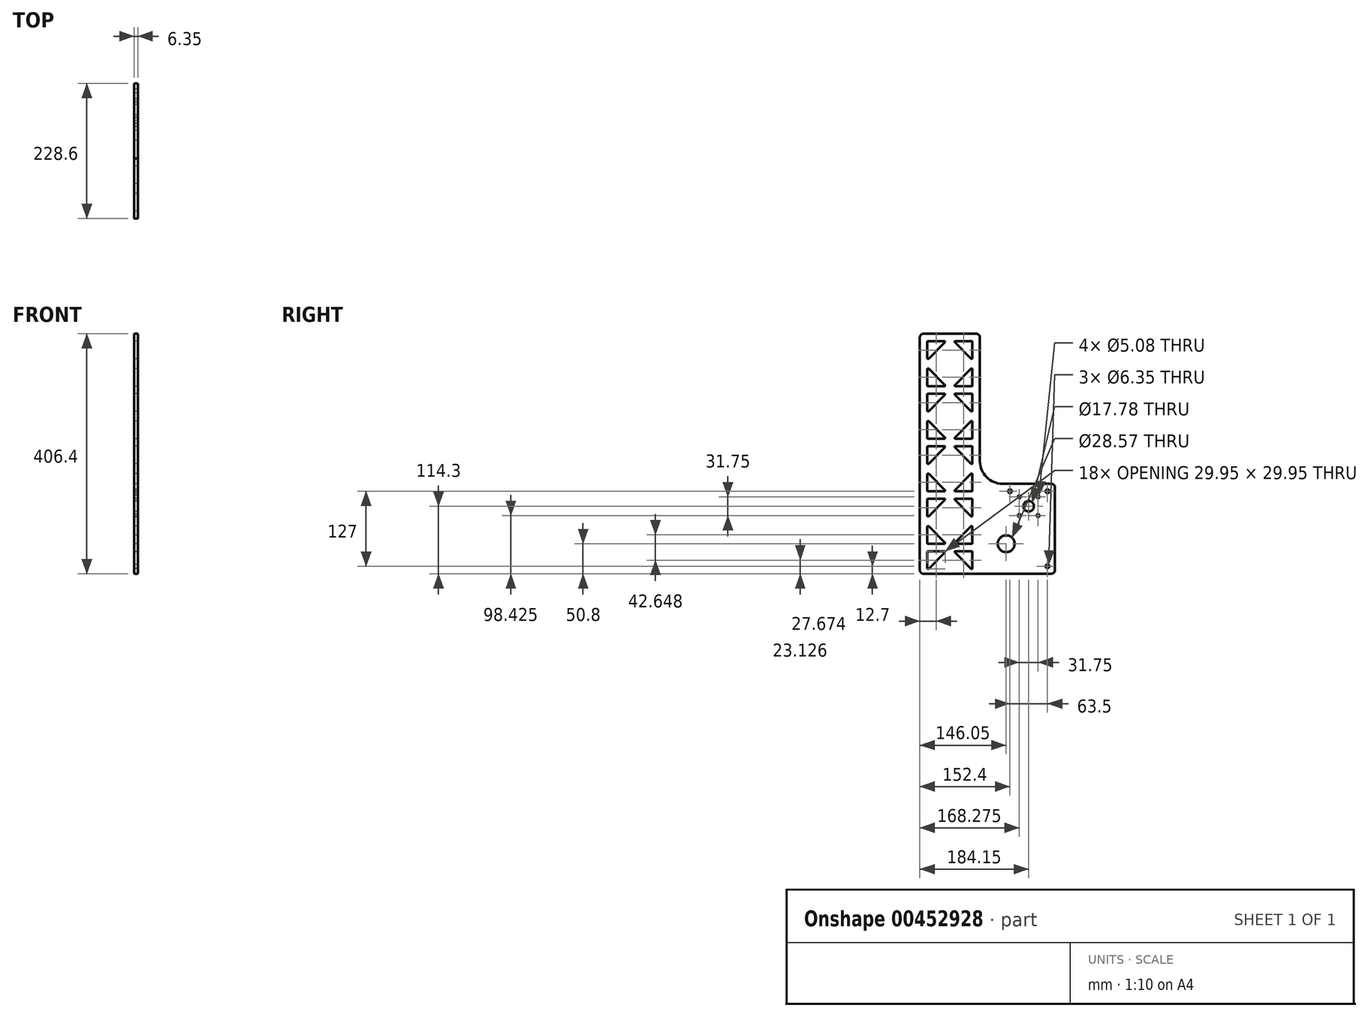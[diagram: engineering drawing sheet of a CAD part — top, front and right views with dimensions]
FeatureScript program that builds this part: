
annotation { "Feature Type Name" : "Feature", "Feature Type Description" : "" }
export const myFeature = defineFeature(function(context is Context, id is Id, definition is map)
    precondition{}
    {
        {
            var Q0;
            Q0=qCreatedBy(makeId("Right.planeOp"),FACE);
            var sketch = newSketch(context, id + "F0", { "sketchPlane" : qUnion([Q0])});
            skLineSegment(sketch, "E0.bottom", {"start": v(0, 0) * mm, "end": v(101.6, 0) * mm});
            skLineSegment(sketch, "E0.top", {"start": v(0, 406.4) * mm, "end": v(101.6, 406.4) * mm});
            skLineSegment(sketch, "E0.left", {"start": v(0, 0) * mm, "end": v(0, 406.4) * mm});
            skLineSegment(sketch, "E0.right", {"start": v(101.6, 0) * mm, "end": v(101.6, 406.4) * mm});
            skLineSegment(sketch, "E1.bottom", {"start": v(101.6, 0) * mm, "end": v(228.6, 0) * mm});
            skLineSegment(sketch, "E1.top", {"start": v(101.6, 152.4) * mm, "end": v(228.6, 152.4) * mm});
            skLineSegment(sketch, "E1.left", {"start": v(101.6, 0) * mm, "end": v(101.6, 152.4) * mm});
            skLineSegment(sketch, "E1.right", {"start": v(228.6, 0) * mm, "end": v(228.6, 152.4) * mm});
            skCircle(sketch, "E2", {"center": v(146.05, 50.8) * mm, "radius": 14.29 * mm});
            skCircle(sketch, "E3", {"center": v(146.05, 50.8) * mm, "radius": 50.8 * mm, "construction": true});
            skCircle(sketch, "E4", {"center": v(215.9, 12.7) * mm, "radius": 3.18 * mm});
            skCircle(sketch, "E5", {"center": v(215.9, 139.7) * mm, "radius": 3.18 * mm});
            skLineSegment(sketch, "E6", {"start": v(87.63, 393.7) * mm, "end": v(60.22, 393.7) * mm});
            skLineSegment(sketch, "E7", {"start": v(59.32, 391.53) * mm, "end": v(86.73, 364.12) * mm});
            skLineSegment(sketch, "E8", {"start": v(88.9, 365.02) * mm, "end": v(88.9, 392.43) * mm});
            skPoint(sketch, "E9.visualSharp", {"position": v(57.15, 393.7) * mm});
            skArc(sketch, "E9.filletArc", {"start": v(60.22, 393.7) * mm, "mid": v(59.04, 392.92) * mm, "end": v(59.32, 391.53) * mm});
            skPoint(sketch, "E10.visualSharp", {"position": v(88.9, 361.95) * mm});
            skArc(sketch, "E11.filletArc", {"start": v(86.73, 364.12) * mm, "mid": v(88.12, 363.84) * mm, "end": v(88.9, 365.02) * mm});
            skPoint(sketch, "E12.visualSharp", {"position": v(88.9, 393.7) * mm});
            skArc(sketch, "E12.filletArc", {"start": v(88.9, 392.43) * mm, "mid": v(88.53, 393.33) * mm, "end": v(87.63, 393.7) * mm});
            skPoint(sketch, "E13.startSnap0", {"position": v(50.8, 406.4) * mm});
            skLineSegment(sketch, "E14", {"start": v(50.8, 406.4) * mm, "end": v(50.8, -18.77) * mm, "construction": true});
            skPoint(sketch, "E14.endSnap0", {"position": v(50.8, 0) * mm});
            skArc(sketch, "E15.MirrorCS", {"start": v(12.7, 392.43) * mm, "mid": v(13.07, 393.33) * mm, "end": v(13.97, 393.7) * mm});
            skArc(sketch, "E16.MirrorCS", {"start": v(41.38, 393.7) * mm, "mid": v(42.56, 392.92) * mm, "end": v(42.28, 391.53) * mm});
            skPoint(sketch, "E17.MirrorP", {"position": v(12.7, 361.95) * mm});
            skLineSegment(sketch, "E18.MirrorCS", {"start": v(13.97, 393.7) * mm, "end": v(41.38, 393.7) * mm});
            skPoint(sketch, "E19.MirrorP", {"position": v(12.7, 393.7) * mm});
            skLineSegment(sketch, "E20.MirrorCS", {"start": v(42.28, 391.53) * mm, "end": v(14.87, 364.12) * mm});
            skPoint(sketch, "E21.MirrorP", {"position": v(44.45, 393.7) * mm});
            skArc(sketch, "E22.MirrorCS", {"start": v(14.87, 364.12) * mm, "mid": v(13.48, 363.84) * mm, "end": v(12.7, 365.02) * mm});
            skLineSegment(sketch, "E23.MirrorCS", {"start": v(12.7, 365.02) * mm, "end": v(12.7, 392.43) * mm});
            skLineSegment(sketch, "E24", {"start": v(-14.42, 355.6) * mm, "end": v(137.53, 355.6) * mm, "construction": true});
            skArc(sketch, "E25.MirrorCS", {"start": v(12.7, 318.77) * mm, "mid": v(13.07, 317.87) * mm, "end": v(13.97, 317.5) * mm});
            skArc(sketch, "E26.MirrorCS", {"start": v(60.22, 317.5) * mm, "mid": v(59.04, 318.28) * mm, "end": v(59.32, 319.67) * mm});
            skArc(sketch, "E27.MirrorCS", {"start": v(14.87, 347.08) * mm, "mid": v(13.48, 347.36) * mm, "end": v(12.7, 346.18) * mm});
            skArc(sketch, "E28.MirrorCS", {"start": v(41.38, 317.5) * mm, "mid": v(42.56, 318.28) * mm, "end": v(42.28, 319.67) * mm});
            skArc(sketch, "E29.MirrorCS", {"start": v(86.73, 347.08) * mm, "mid": v(88.12, 347.36) * mm, "end": v(88.9, 346.18) * mm});
            skArc(sketch, "E30.MirrorCS", {"start": v(88.9, 318.77) * mm, "mid": v(88.53, 317.87) * mm, "end": v(87.63, 317.5) * mm});
            skPoint(sketch, "E31.MirrorP", {"position": v(12.7, 349.25) * mm});
            skPoint(sketch, "E32.MirrorP", {"position": v(88.9, 349.25) * mm});
            skPoint(sketch, "E33.MirrorP", {"position": v(12.7, 317.5) * mm});
            skPoint(sketch, "E34.MirrorP", {"position": v(44.45, 317.5) * mm});
            skLineSegment(sketch, "E35.MirrorCS", {"start": v(50.8, 304.8) * mm, "end": v(50.8, 729.97) * mm, "construction": true});
            skPoint(sketch, "E36.MirrorP", {"position": v(88.9, 317.5) * mm});
            skLineSegment(sketch, "E37.MirrorCS", {"start": v(12.7, 346.18) * mm, "end": v(12.7, 318.77) * mm});
            skLineSegment(sketch, "E38.MirrorCS", {"start": v(88.9, 346.18) * mm, "end": v(88.9, 318.77) * mm});
            skLineSegment(sketch, "E39.MirrorCS", {"start": v(42.28, 319.67) * mm, "end": v(14.87, 347.08) * mm});
            skLineSegment(sketch, "E40.MirrorCS", {"start": v(13.97, 317.5) * mm, "end": v(41.38, 317.5) * mm});
            skPoint(sketch, "E41.MirrorP", {"position": v(57.15, 317.5) * mm});
            skLineSegment(sketch, "E42.MirrorCS", {"start": v(87.63, 317.5) * mm, "end": v(60.22, 317.5) * mm});
            skLineSegment(sketch, "E43.MirrorCS", {"start": v(59.32, 319.67) * mm, "end": v(86.73, 347.08) * mm});
            skPoint(sketch, "E44.0.1.0", {"position": v(44.45, 304.8) * mm});
            skLineSegment(sketch, "E44.0.1.1", {"start": v(12.7, 276.12) * mm, "end": v(12.7, 303.53) * mm});
            skPoint(sketch, "E44.0.1.2", {"position": v(12.7, 273.05) * mm});
            skPoint(sketch, "E44.0.1.3", {"position": v(12.7, 304.8) * mm});
            skLineSegment(sketch, "E44.0.1.4", {"start": v(42.28, 302.63) * mm, "end": v(14.87, 275.22) * mm});
            skLineSegment(sketch, "E44.0.1.5", {"start": v(13.97, 304.8) * mm, "end": v(41.38, 304.8) * mm});
            skPoint(sketch, "E44.0.1.6", {"position": v(12.7, 273.05) * mm});
            skArc(sketch, "E44.0.1.7", {"start": v(14.87, 275.22) * mm, "mid": v(13.48, 274.94) * mm, "end": v(12.7, 276.12) * mm});
            skArc(sketch, "E44.0.1.8", {"start": v(41.38, 304.8) * mm, "mid": v(42.56, 304.02) * mm, "end": v(42.28, 302.63) * mm});
            skArc(sketch, "E44.0.1.9", {"start": v(12.7, 303.53) * mm, "mid": v(13.07, 304.43) * mm, "end": v(13.97, 304.8) * mm});
            skPoint(sketch, "E44.0.1.10", {"position": v(44.45, 228.6) * mm});
            skLineSegment(sketch, "E44.0.1.11", {"start": v(13.97, 228.6) * mm, "end": v(41.38, 228.6) * mm});
            skPoint(sketch, "E44.0.1.12", {"position": v(12.7, 260.35) * mm});
            skLineSegment(sketch, "E44.0.1.13", {"start": v(42.28, 230.77) * mm, "end": v(14.87, 258.18) * mm});
            skPoint(sketch, "E44.0.1.14", {"position": v(12.7, 228.6) * mm});
            skLineSegment(sketch, "E44.0.1.15", {"start": v(12.7, 257.28) * mm, "end": v(12.7, 229.87) * mm});
            skPoint(sketch, "E44.0.1.16", {"position": v(12.7, 260.35) * mm});
            skArc(sketch, "E44.0.1.17", {"start": v(41.38, 228.6) * mm, "mid": v(42.56, 229.38) * mm, "end": v(42.28, 230.77) * mm});
            skArc(sketch, "E44.0.1.18", {"start": v(14.87, 258.18) * mm, "mid": v(13.48, 258.46) * mm, "end": v(12.7, 257.28) * mm});
            skArc(sketch, "E44.0.1.19", {"start": v(12.7, 229.87) * mm, "mid": v(13.07, 228.97) * mm, "end": v(13.97, 228.6) * mm});
            skPoint(sketch, "E44.0.1.20", {"position": v(57.15, 228.6) * mm});
            skPoint(sketch, "E44.0.1.21", {"position": v(88.9, 228.6) * mm});
            skLineSegment(sketch, "E44.0.1.22", {"start": v(59.32, 230.77) * mm, "end": v(86.73, 258.18) * mm});
            skLineSegment(sketch, "E44.0.1.23", {"start": v(87.63, 228.6) * mm, "end": v(60.22, 228.6) * mm});
            skPoint(sketch, "E44.0.1.24", {"position": v(88.9, 260.35) * mm});
            skLineSegment(sketch, "E44.0.1.25", {"start": v(88.9, 257.28) * mm, "end": v(88.9, 229.87) * mm});
            skPoint(sketch, "E44.0.1.26", {"position": v(88.9, 260.35) * mm});
            skArc(sketch, "E44.0.1.27", {"start": v(60.22, 228.6) * mm, "mid": v(59.04, 229.38) * mm, "end": v(59.32, 230.77) * mm});
            skArc(sketch, "E44.0.1.28", {"start": v(88.9, 229.87) * mm, "mid": v(88.53, 228.97) * mm, "end": v(87.63, 228.6) * mm});
            skArc(sketch, "E44.0.1.29", {"start": v(86.73, 258.18) * mm, "mid": v(88.12, 258.46) * mm, "end": v(88.9, 257.28) * mm});
            skLineSegment(sketch, "E44.0.1.30", {"start": v(88.9, 276.12) * mm, "end": v(88.9, 303.53) * mm});
            skLineSegment(sketch, "E44.0.1.31", {"start": v(59.32, 302.63) * mm, "end": v(86.73, 275.22) * mm});
            skLineSegment(sketch, "E44.0.1.32", {"start": v(87.63, 304.8) * mm, "end": v(60.22, 304.8) * mm});
            skPoint(sketch, "E44.0.1.33", {"position": v(88.9, 304.8) * mm});
            skPoint(sketch, "E44.0.1.34", {"position": v(88.9, 273.05) * mm});
            skPoint(sketch, "E44.0.1.35", {"position": v(57.15, 304.8) * mm});
            skPoint(sketch, "E44.0.1.36", {"position": v(88.9, 273.05) * mm});
            skArc(sketch, "E44.0.1.37", {"start": v(86.73, 275.22) * mm, "mid": v(88.12, 274.94) * mm, "end": v(88.9, 276.12) * mm});
            skArc(sketch, "E44.0.1.38", {"start": v(88.9, 303.53) * mm, "mid": v(88.53, 304.43) * mm, "end": v(87.63, 304.8) * mm});
            skArc(sketch, "E44.0.1.39", {"start": v(60.22, 304.8) * mm, "mid": v(59.04, 304.02) * mm, "end": v(59.32, 302.63) * mm});
            skPoint(sketch, "E44.0.2.0", {"position": v(44.45, 215.9) * mm});
            skLineSegment(sketch, "E44.0.2.1", {"start": v(12.7, 187.22) * mm, "end": v(12.7, 214.63) * mm});
            skPoint(sketch, "E44.0.2.2", {"position": v(12.7, 184.15) * mm});
            skPoint(sketch, "E44.0.2.3", {"position": v(12.7, 215.9) * mm});
            skLineSegment(sketch, "E44.0.2.4", {"start": v(42.28, 213.73) * mm, "end": v(14.87, 186.32) * mm});
            skLineSegment(sketch, "E44.0.2.5", {"start": v(13.97, 215.9) * mm, "end": v(41.38, 215.9) * mm});
            skPoint(sketch, "E44.0.2.6", {"position": v(12.7, 184.15) * mm});
            skArc(sketch, "E44.0.2.7", {"start": v(14.87, 186.32) * mm, "mid": v(13.48, 186.04) * mm, "end": v(12.7, 187.22) * mm});
            skArc(sketch, "E44.0.2.8", {"start": v(41.38, 215.9) * mm, "mid": v(42.56, 215.12) * mm, "end": v(42.28, 213.73) * mm});
            skArc(sketch, "E44.0.2.9", {"start": v(12.7, 214.63) * mm, "mid": v(13.07, 215.53) * mm, "end": v(13.97, 215.9) * mm});
            skPoint(sketch, "E44.0.2.10", {"position": v(44.45, 139.7) * mm});
            skLineSegment(sketch, "E44.0.2.11", {"start": v(13.97, 139.7) * mm, "end": v(41.38, 139.7) * mm});
            skPoint(sketch, "E44.0.2.12", {"position": v(12.7, 171.45) * mm});
            skLineSegment(sketch, "E44.0.2.13", {"start": v(42.28, 141.87) * mm, "end": v(14.87, 169.28) * mm});
            skPoint(sketch, "E44.0.2.14", {"position": v(12.7, 139.7) * mm});
            skLineSegment(sketch, "E44.0.2.15", {"start": v(12.7, 168.38) * mm, "end": v(12.7, 140.97) * mm});
            skPoint(sketch, "E44.0.2.16", {"position": v(12.7, 171.45) * mm});
            skArc(sketch, "E44.0.2.17", {"start": v(41.38, 139.7) * mm, "mid": v(42.56, 140.48) * mm, "end": v(42.28, 141.87) * mm});
            skArc(sketch, "E44.0.2.18", {"start": v(14.87, 169.28) * mm, "mid": v(13.48, 169.56) * mm, "end": v(12.7, 168.38) * mm});
            skArc(sketch, "E44.0.2.19", {"start": v(12.7, 140.97) * mm, "mid": v(13.07, 140.07) * mm, "end": v(13.97, 139.7) * mm});
            skPoint(sketch, "E44.0.2.20", {"position": v(57.15, 139.7) * mm});
            skPoint(sketch, "E44.0.2.21", {"position": v(88.9, 139.7) * mm});
            skLineSegment(sketch, "E44.0.2.22", {"start": v(59.32, 141.87) * mm, "end": v(86.73, 169.28) * mm});
            skLineSegment(sketch, "E44.0.2.23", {"start": v(87.63, 139.7) * mm, "end": v(60.22, 139.7) * mm});
            skPoint(sketch, "E44.0.2.24", {"position": v(88.9, 171.45) * mm});
            skLineSegment(sketch, "E44.0.2.25", {"start": v(88.9, 168.38) * mm, "end": v(88.9, 140.97) * mm});
            skPoint(sketch, "E44.0.2.26", {"position": v(88.9, 171.45) * mm});
            skArc(sketch, "E44.0.2.27", {"start": v(60.22, 139.7) * mm, "mid": v(59.04, 140.48) * mm, "end": v(59.32, 141.87) * mm});
            skArc(sketch, "E44.0.2.28", {"start": v(88.9, 140.97) * mm, "mid": v(88.53, 140.07) * mm, "end": v(87.63, 139.7) * mm});
            skArc(sketch, "E44.0.2.29", {"start": v(86.73, 169.28) * mm, "mid": v(88.12, 169.56) * mm, "end": v(88.9, 168.38) * mm});
            skLineSegment(sketch, "E44.0.2.30", {"start": v(88.9, 187.22) * mm, "end": v(88.9, 214.63) * mm});
            skLineSegment(sketch, "E44.0.2.31", {"start": v(59.32, 213.73) * mm, "end": v(86.73, 186.32) * mm});
            skLineSegment(sketch, "E44.0.2.32", {"start": v(87.63, 215.9) * mm, "end": v(60.22, 215.9) * mm});
            skPoint(sketch, "E44.0.2.33", {"position": v(88.9, 215.9) * mm});
            skPoint(sketch, "E44.0.2.34", {"position": v(88.9, 184.15) * mm});
            skPoint(sketch, "E44.0.2.35", {"position": v(57.15, 215.9) * mm});
            skPoint(sketch, "E44.0.2.36", {"position": v(88.9, 184.15) * mm});
            skArc(sketch, "E44.0.2.37", {"start": v(86.73, 186.32) * mm, "mid": v(88.12, 186.04) * mm, "end": v(88.9, 187.22) * mm});
            skArc(sketch, "E44.0.2.38", {"start": v(88.9, 214.63) * mm, "mid": v(88.53, 215.53) * mm, "end": v(87.63, 215.9) * mm});
            skArc(sketch, "E44.0.2.39", {"start": v(60.22, 215.9) * mm, "mid": v(59.04, 215.12) * mm, "end": v(59.32, 213.73) * mm});
            skLineSegment(sketch, "E44.direction1", {"start": v(12.7, 317.5) * mm, "end": v(12.65, 317.5) * mm, "construction": true});
            skLineSegment(sketch, "E44.direction2", {"start": v(12.7, 317.5) * mm, "end": v(12.7, 228.6) * mm, "construction": true});
            skPoint(sketch, "E45.0.0.3", {"position": v(44.45, 127) * mm});
            skLineSegment(sketch, "E45.1.0.3", {"start": v(12.7, 98.32) * mm, "end": v(12.7, 125.73) * mm});
            skPoint(sketch, "E45.4.0.3", {"position": v(12.7, 95.25) * mm});
            skPoint(sketch, "E45.5.0.3", {"position": v(12.7, 127) * mm});
            skLineSegment(sketch, "E45.6.0.3", {"start": v(42.28, 124.83) * mm, "end": v(14.87, 97.42) * mm});
            skLineSegment(sketch, "E45.9.0.3", {"start": v(13.97, 127) * mm, "end": v(41.38, 127) * mm});
            skPoint(sketch, "E45.12.0.3", {"position": v(12.7, 95.25) * mm});
            skArc(sketch, "E45.13.0.3", {"start": v(14.87, 97.42) * mm, "mid": v(13.48, 97.14) * mm, "end": v(12.7, 98.32) * mm});
            skArc(sketch, "E45.17.0.3", {"start": v(41.38, 127) * mm, "mid": v(42.56, 126.22) * mm, "end": v(42.28, 124.83) * mm});
            skArc(sketch, "E45.21.0.3", {"start": v(12.7, 125.73) * mm, "mid": v(13.07, 126.63) * mm, "end": v(13.97, 127) * mm});
            skPoint(sketch, "E45.25.0.3", {"position": v(44.45, 50.8) * mm});
            skLineSegment(sketch, "E45.26.0.3", {"start": v(13.97, 50.8) * mm, "end": v(41.38, 50.8) * mm});
            skPoint(sketch, "E45.29.0.3", {"position": v(12.7, 82.55) * mm});
            skLineSegment(sketch, "E45.30.0.3", {"start": v(42.28, 52.97) * mm, "end": v(14.87, 80.38) * mm});
            skPoint(sketch, "E45.33.0.3", {"position": v(12.7, 50.8) * mm});
            skLineSegment(sketch, "E45.34.0.3", {"start": v(12.7, 79.48) * mm, "end": v(12.7, 52.07) * mm});
            skPoint(sketch, "E45.37.0.3", {"position": v(12.7, 82.55) * mm});
            skArc(sketch, "E45.38.0.3", {"start": v(41.38, 50.8) * mm, "mid": v(42.56, 51.58) * mm, "end": v(42.28, 52.97) * mm});
            skArc(sketch, "E45.42.0.3", {"start": v(14.87, 80.38) * mm, "mid": v(13.48, 80.66) * mm, "end": v(12.7, 79.48) * mm});
            skArc(sketch, "E45.46.0.3", {"start": v(12.7, 52.07) * mm, "mid": v(13.07, 51.17) * mm, "end": v(13.97, 50.8) * mm});
            skPoint(sketch, "E45.50.0.3", {"position": v(57.15, 50.8) * mm});
            skPoint(sketch, "E45.51.0.3", {"position": v(88.9, 50.8) * mm});
            skLineSegment(sketch, "E45.52.0.3", {"start": v(59.32, 52.97) * mm, "end": v(86.73, 80.38) * mm});
            skLineSegment(sketch, "E45.55.0.3", {"start": v(87.63, 50.8) * mm, "end": v(60.22, 50.8) * mm});
            skPoint(sketch, "E45.58.0.3", {"position": v(88.9, 82.55) * mm});
            skLineSegment(sketch, "E45.59.0.3", {"start": v(88.9, 79.48) * mm, "end": v(88.9, 52.07) * mm});
            skPoint(sketch, "E45.62.0.3", {"position": v(88.9, 82.55) * mm});
            skArc(sketch, "E45.63.0.3", {"start": v(60.22, 50.8) * mm, "mid": v(59.04, 51.58) * mm, "end": v(59.32, 52.97) * mm});
            skArc(sketch, "E45.67.0.3", {"start": v(88.9, 52.07) * mm, "mid": v(88.53, 51.17) * mm, "end": v(87.63, 50.8) * mm});
            skArc(sketch, "E45.71.0.3", {"start": v(86.73, 80.38) * mm, "mid": v(88.12, 80.66) * mm, "end": v(88.9, 79.48) * mm});
            skLineSegment(sketch, "E45.75.0.3", {"start": v(88.9, 98.32) * mm, "end": v(88.9, 125.73) * mm});
            skLineSegment(sketch, "E45.78.0.3", {"start": v(59.32, 124.83) * mm, "end": v(86.73, 97.42) * mm});
            skLineSegment(sketch, "E45.81.0.3", {"start": v(87.63, 127) * mm, "end": v(60.22, 127) * mm});
            skPoint(sketch, "E45.84.0.3", {"position": v(88.9, 127) * mm});
            skPoint(sketch, "E45.85.0.3", {"position": v(88.9, 95.25) * mm});
            skPoint(sketch, "E45.86.0.3", {"position": v(57.15, 127) * mm});
            skPoint(sketch, "E45.87.0.3", {"position": v(88.9, 95.25) * mm});
            skArc(sketch, "E45.88.0.3", {"start": v(86.73, 97.42) * mm, "mid": v(88.12, 97.14) * mm, "end": v(88.9, 98.32) * mm});
            skArc(sketch, "E45.92.0.3", {"start": v(88.9, 125.73) * mm, "mid": v(88.53, 126.63) * mm, "end": v(87.63, 127) * mm});
            skArc(sketch, "E45.96.0.3", {"start": v(60.22, 127) * mm, "mid": v(59.04, 126.22) * mm, "end": v(59.32, 124.83) * mm});
            skPoint(sketch, "E45.0.0.4", {"position": v(44.45, 38.1) * mm});
            skLineSegment(sketch, "E45.1.0.4", {"start": v(12.7, 9.42) * mm, "end": v(12.7, 36.83) * mm});
            skPoint(sketch, "E45.4.0.4", {"position": v(12.7, 6.35) * mm});
            skPoint(sketch, "E45.5.0.4", {"position": v(12.7, 38.1) * mm});
            skLineSegment(sketch, "E45.6.0.4", {"start": v(42.28, 35.93) * mm, "end": v(14.87, 8.52) * mm});
            skLineSegment(sketch, "E45.9.0.4", {"start": v(13.97, 38.1) * mm, "end": v(41.38, 38.1) * mm});
            skPoint(sketch, "E45.12.0.4", {"position": v(12.7, 6.35) * mm});
            skArc(sketch, "E45.13.0.4", {"start": v(14.87, 8.52) * mm, "mid": v(13.48, 8.24) * mm, "end": v(12.7, 9.42) * mm});
            skArc(sketch, "E45.17.0.4", {"start": v(41.38, 38.1) * mm, "mid": v(42.56, 37.32) * mm, "end": v(42.28, 35.93) * mm});
            skArc(sketch, "E45.21.0.4", {"start": v(12.7, 36.83) * mm, "mid": v(13.07, 37.73) * mm, "end": v(13.97, 38.1) * mm});
            skLineSegment(sketch, "E45.75.0.4", {"start": v(88.9, 9.42) * mm, "end": v(88.9, 36.83) * mm});
            skLineSegment(sketch, "E45.78.0.4", {"start": v(59.32, 35.93) * mm, "end": v(86.73, 8.52) * mm});
            skLineSegment(sketch, "E45.81.0.4", {"start": v(87.63, 38.1) * mm, "end": v(60.22, 38.1) * mm});
            skPoint(sketch, "E45.84.0.4", {"position": v(88.9, 38.1) * mm});
            skPoint(sketch, "E45.85.0.4", {"position": v(88.9, 6.35) * mm});
            skPoint(sketch, "E45.86.0.4", {"position": v(57.15, 38.1) * mm});
            skPoint(sketch, "E45.87.0.4", {"position": v(88.9, 6.35) * mm});
            skArc(sketch, "E45.88.0.4", {"start": v(86.73, 8.52) * mm, "mid": v(88.12, 8.24) * mm, "end": v(88.9, 9.42) * mm});
            skArc(sketch, "E45.92.0.4", {"start": v(88.9, 36.83) * mm, "mid": v(88.53, 37.73) * mm, "end": v(87.63, 38.1) * mm});
            skArc(sketch, "E45.96.0.4", {"start": v(60.22, 38.1) * mm, "mid": v(59.04, 37.32) * mm, "end": v(59.32, 35.93) * mm});
            skArc(sketch, "E46", {"start": v(101.6, 190.5) * mm, "mid": v(112.76, 163.56) * mm, "end": v(139.7, 152.4) * mm});
            skLineSegment(sketch, "E47", {"start": v(139.7, 190.5) * mm, "end": v(101.6, 190.5) * mm});
            skCircle(sketch, "E48", {"center": v(215.9, 139.7) * mm, "radius": 6.35 * mm, "construction": true});
            skCircle(sketch, "E49", {"center": v(152.4, 139.7) * mm, "radius": 3.18 * mm});
            skCircle(sketch, "E50", {"center": v(152.4, 139.7) * mm, "radius": 6.35 * mm, "construction": true});
            skCircle(sketch, "E51", {"center": v(215.9, 12.7) * mm, "radius": 6.35 * mm, "construction": true});
            skCircle(sketch, "E52", {"center": v(184.15, 114.3) * mm, "radius": 8.9 * mm});
            skLineSegment(sketch, "E53.bottom", {"start": v(200.03, 130.17) * mm, "end": v(168.28, 130.17) * mm, "construction": true});
            skLineSegment(sketch, "E53.top", {"start": v(200.03, 98.43) * mm, "end": v(168.28, 98.43) * mm, "construction": true});
            skLineSegment(sketch, "E53.left", {"start": v(200.03, 130.17) * mm, "end": v(200.03, 98.43) * mm, "construction": true});
            skLineSegment(sketch, "E53.right", {"start": v(168.28, 130.17) * mm, "end": v(168.28, 98.43) * mm, "construction": true});
            skCircle(sketch, "E54", {"center": v(168.28, 98.43) * mm, "radius": 2.54 * mm});
            skCircle(sketch, "E55", {"center": v(200.03, 98.43) * mm, "radius": 2.54 * mm});
            skCircle(sketch, "E56", {"center": v(168.28, 130.17) * mm, "radius": 2.54 * mm});
            skCircle(sketch, "E57", {"center": v(200.03, 130.17) * mm, "radius": 2.54 * mm});
            skSolve(sketch);
        }
        {
            var Q0;
            Q0=makeQuery(id+"F0.imprint","IMPRINT",FACE,{"disambiguationData":[TD([[makeQuery(id+"F0.imprint","IMPRINT",EDGE,{"derivedFrom":sQuery(id+"F0.wireOp",EDGE,"E0.bottom")}),1.0]])]});
            var Q1;
            Q1=makeQuery(id+"F0.imprint","IMPRINT",FACE,{"disambiguationData":[TD([[makeQuery(id+"F0.imprint","IMPRINT",EDGE,{"derivedFrom":sQuery(id+"F0.wireOp",EDGE,"E1.bottom")}),1.0]])]});
            var Q2;
            {var subQ3=sQuery(id+"F0.wireOp",EDGE,"E46");Q2=makeQuery(id+"F0.imprint","IMPRINT",FACE,{"disambiguationData":[TD([[makeQuery(id+"F0.imprint","IMPRINT",EDGE,{"derivedFrom":subQ3}),-1.0]])]});}
            extrude(context, id + "F1", {"entities" : qUnion([Q0, Q1, Q2]), "depth" : 6.35 * mm});
        }
        {
            var Q0;
            Q0=makeQuery(id+"F1.opExtrude","SWEPT_EDGE",EDGE,{"disambiguationData":[OSD([sQuery(id+"F0.wireOp",EDGE,"E1.bottom"),sQuery(id+"F0.wireOp",EDGE,"E1.right")])]});
            var Q1;
            Q1=makeQuery(id+"F1.opExtrude","SWEPT_EDGE",EDGE,{"disambiguationData":[OSD([sQuery(id+"F0.wireOp",EDGE,"E1.top"),sQuery(id+"F0.wireOp",EDGE,"E1.right")])]});
            var Q2;
            Q2=makeQuery(id+"F1.opExtrude","SWEPT_EDGE",EDGE,{"disambiguationData":[OSD([sQuery(id+"F0.wireOp",EDGE,"E0.bottom"),sQuery(id+"F0.wireOp",EDGE,"E0.left")])]});
            var Q3;
            Q3=makeQuery(id+"F1.opExtrude","SWEPT_EDGE",EDGE,{"disambiguationData":[OSD([sQuery(id+"F0.wireOp",EDGE,"E0.top"),sQuery(id+"F0.wireOp",EDGE,"E0.left")])]});
            var Q4;
            Q4=makeQuery(id+"F1.opExtrude","SWEPT_EDGE",EDGE,{"disambiguationData":[OSD([sQuery(id+"F0.wireOp",EDGE,"E0.top"),sQuery(id+"F0.wireOp",EDGE,"E0.right")])]});
            fillet(context, id + "F2", {"entities" : qUnion([Q0, Q1, Q2, Q3, Q4]), "radius" : 6.35 * mm, "tangentPropagation" : true, "allowEdgeOverflow" : false});
        }
    });
